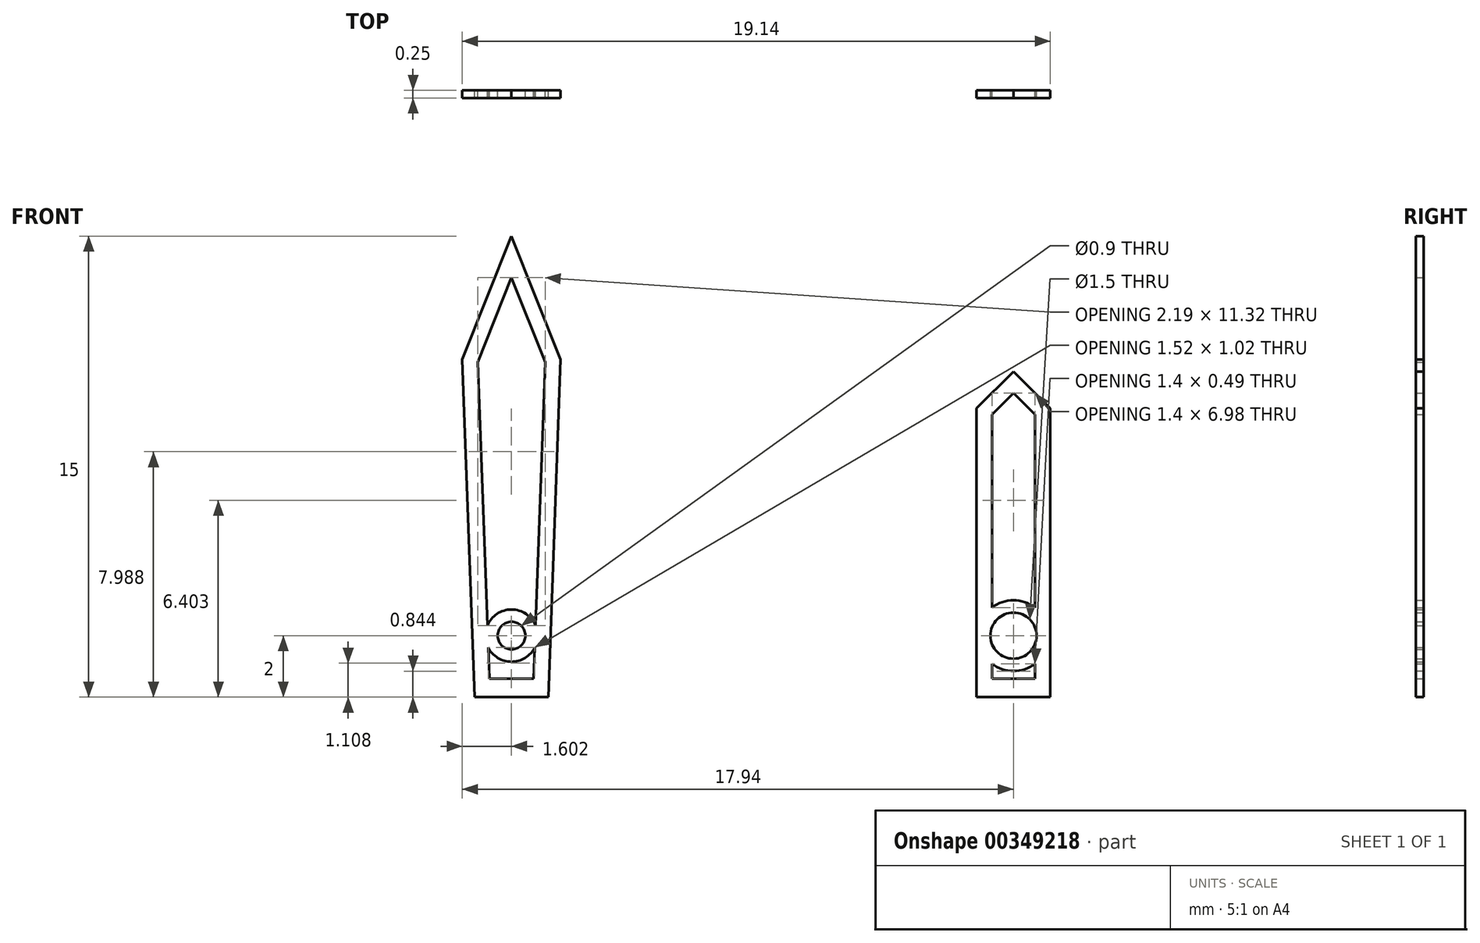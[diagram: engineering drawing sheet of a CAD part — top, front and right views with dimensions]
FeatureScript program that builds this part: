
annotation { "Feature Type Name" : "Feature", "Feature Type Description" : "" }
export const myFeature = defineFeature(function(context is Context, id is Id, definition is map)
    precondition{}
    {
        {
            var Q0;
            Q0=qCreatedBy(makeId("Front.planeOp"),FACE);
            var sketch = newSketch(context, id + "F0", { "sketchPlane" : qUnion([Q0])});
            skLineSegment(sketch, "E0", {"start": v(-36.59, 13) * mm, "end": v(-34.99, 8.98) * mm});
            skCircle(sketch, "E1", {"center": v(-36.59, 0) * mm, "radius": 0.45 * mm});
            skCircle(sketch, "E2.0", {"center": v(-36.59, 0) * mm, "radius": 0.85 * mm});
            skCircle(sketch, "E3", {"center": v(-20.25, 0) * mm, "radius": 0.75 * mm});
            skCircle(sketch, "E4", {"center": v(-28.42, 0) * mm, "radius": 0.35 * mm});
            skCircle(sketch, "E5", {"center": v(-28.42, 0) * mm, "radius": 0.75 * mm});
            skLineSegment(sketch, "E6", {"start": v(-20.25, 0) * mm, "end": v(-36.59, 0) * mm});
            skLineSegment(sketch, "E7", {"start": v(-36.59, 13) * mm, "end": v(-36.59, 0) * mm});
            skLineSegment(sketch, "E8.MirrorCS", {"start": v(-36.59, 13) * mm, "end": v(-38.19, 8.98) * mm});
            skLineSegment(sketch, "E9", {"start": v(-28.42, 0) * mm, "end": v(-28.42, 13) * mm});
            skLineSegment(sketch, "E10.0", {"start": v(-28.12, 0) * mm, "end": v(-28.12, 13) * mm});
            skLineSegment(sketch, "E11.MirrorCS", {"start": v(-28.72, 0) * mm, "end": v(-28.72, 13) * mm});
            skLineSegment(sketch, "E12", {"start": v(-28.72, 13) * mm, "end": v(-28.12, 13) * mm});
            skLineSegment(sketch, "E13.MirrorCS", {"start": v(-28.12, 0) * mm, "end": v(-28.12, -13) * mm});
            skLineSegment(sketch, "E14.MirrorCS", {"start": v(-28.72, 0) * mm, "end": v(-28.72, -13) * mm});
            skLineSegment(sketch, "E15.MirrorCS", {"start": v(-28.72, -13) * mm, "end": v(-28.12, -13) * mm});
            skLineSegment(sketch, "E16", {"start": v(-28.42, 0) * mm, "end": v(-28.42, -13) * mm});
            skLineSegment(sketch, "E17", {"start": v(-19.05, 1.5) * mm, "end": v(-19.05, 7.4) * mm});
            skLineSegment(sketch, "E18", {"start": v(-19.05, 7.4) * mm, "end": v(-20.25, 8.6) * mm});
            skLineSegment(sketch, "E19", {"start": v(-20.25, 7.9) * mm, "end": v(-19.55, 7.2) * mm});
            skLineSegment(sketch, "E20", {"start": v(-19.55, 7.2) * mm, "end": v(-19.55, 1.5) * mm});
            skLineSegment(sketch, "E21.MirrorCS", {"start": v(-20.25, 7.9) * mm, "end": v(-20.95, 7.2) * mm});
            skLineSegment(sketch, "E22.MirrorCS", {"start": v(-21.45, 7.4) * mm, "end": v(-20.25, 8.6) * mm});
            skLineSegment(sketch, "E23.MirrorCS", {"start": v(-20.95, 7.2) * mm, "end": v(-20.95, 1.5) * mm});
            skLineSegment(sketch, "E24.MirrorCS", {"start": v(-21.45, 1.5) * mm, "end": v(-21.45, 7.4) * mm});
            skLineSegment(sketch, "E25.bottom", {"start": v(-26.16, 11.7) * mm, "end": v(-23.16, 11.7) * mm});
            skLineSegment(sketch, "E25.top", {"start": v(-26.16, 11.1) * mm, "end": v(-23.16, 11.1) * mm});
            skLineSegment(sketch, "E25.left", {"start": v(-26.16, 11.7) * mm, "end": v(-26.16, 11.1) * mm});
            skLineSegment(sketch, "E25.right", {"start": v(-23.16, 11.7) * mm, "end": v(-23.16, 11.1) * mm});
            skLineSegment(sketch, "E26.bottom", {"start": v(-26.16, 10.1) * mm, "end": v(-23.16, 10.1) * mm});
            skLineSegment(sketch, "E26.top", {"start": v(-26.16, 9.5) * mm, "end": v(-23.16, 9.5) * mm});
            skLineSegment(sketch, "E26.left", {"start": v(-26.16, 10.1) * mm, "end": v(-26.16, 9.5) * mm});
            skLineSegment(sketch, "E26.right", {"start": v(-23.16, 10.1) * mm, "end": v(-23.16, 9.5) * mm});
            skLineSegment(sketch, "E27", {"start": v(-20.25, -2) * mm, "end": v(-19.05, -2) * mm});
            skLineSegment(sketch, "E28", {"start": v(-19.05, -2) * mm, "end": v(-19.05, 1.5) * mm});
            skLineSegment(sketch, "E29.0", {"start": v(-20.25, -1.4) * mm, "end": v(-19.05, -1.4) * mm});
            skLineSegment(sketch, "E30", {"start": v(-19.55, 0.27) * mm, "end": v(-19.55, 1.5) * mm});
            skLineSegment(sketch, "E31", {"start": v(-19.55, -0.27) * mm, "end": v(-19.55, -1.4) * mm});
            skLineSegment(sketch, "E32.MirrorCS", {"start": v(-20.95, 0.27) * mm, "end": v(-20.95, 1.5) * mm});
            skLineSegment(sketch, "E33.MirrorCS", {"start": v(-21.45, -2) * mm, "end": v(-21.45, 1.5) * mm});
            skLineSegment(sketch, "E34.MirrorCS", {"start": v(-20.95, -0.27) * mm, "end": v(-20.95, -1.4) * mm});
            skLineSegment(sketch, "E35.MirrorCS", {"start": v(-20.25, -1.4) * mm, "end": v(-21.45, -1.4) * mm});
            skLineSegment(sketch, "E36.MirrorCS", {"start": v(-20.25, -2) * mm, "end": v(-21.45, -2) * mm});
            skCircle(sketch, "E37", {"center": v(-20.25, 0) * mm, "radius": 1.15 * mm});
            skLineSegment(sketch, "E38", {"start": v(-36.59, -2) * mm, "end": v(-35.39, -2) * mm});
            skLineSegment(sketch, "E39", {"start": v(-34.99, 8.98) * mm, "end": v(-35.39, -2) * mm});
            skLineSegment(sketch, "E40.0", {"start": v(-36.59, -1.4) * mm, "end": v(-35.39, -1.4) * mm});
            skLineSegment(sketch, "E41", {"start": v(-35.5, 8.9) * mm, "end": v(-36.59, 11.65) * mm});
            skLineSegment(sketch, "E42", {"start": v(-35.5, 8.9) * mm, "end": v(-35.8, 0.33) * mm});
            skLineSegment(sketch, "E43", {"start": v(-35.83, -0.38) * mm, "end": v(-35.87, -1.4) * mm});
            skLineSegment(sketch, "E44.MirrorCS", {"start": v(-37.68, 8.9) * mm, "end": v(-36.59, 11.65) * mm});
            skLineSegment(sketch, "E45.MirrorCS", {"start": v(-37.68, 8.9) * mm, "end": v(-37.37, 0.33) * mm});
            skLineSegment(sketch, "E46.MirrorCS", {"start": v(-38.19, 8.98) * mm, "end": v(-37.79, -2) * mm});
            skLineSegment(sketch, "E47.MirrorCS", {"start": v(-36.59, -1.4) * mm, "end": v(-37.79, -1.4) * mm});
            skLineSegment(sketch, "E48.MirrorCS", {"start": v(-36.59, -2) * mm, "end": v(-37.79, -2) * mm});
            skLineSegment(sketch, "E49.MirrorCS", {"start": v(-37.35, -0.38) * mm, "end": v(-37.3, -1.4) * mm});
            skLineSegment(sketch, "E50", {"start": v(-37.68, 8.9) * mm, "end": v(-35.5, 8.9) * mm});
            skLineSegment(sketch, "E51", {"start": v(-20.95, 7.2) * mm, "end": v(-19.55, 7.2) * mm});
            skSolve(sketch);
        }
        {
            var Q0;
            Q0=qSketchRegion(id+"F0",true);
            var Q1;
            {var subQ0=sQuery(id+"F0.wireOp",EDGE,"d177a6a1-e401-462f-85d2-7b86f48335750.MirrorCS");var subQ1=sQuery(id+"F0.wireOp",EDGE,"215cdf59-a4c0-4674-9381-4349cfd28c600.MirrorCS");var subQ2=makeQuery(id+"F0.imprint","INTERSECT",VERTEX,{"derivedFrom":[subQ1,subQ0]});Q1=makeQuery(id+"F0.imprint","IMPRINT",FACE,{"disambiguationData":[TD([[makeQuery(id+"F0.imprint","IMPRINT",EDGE,{"disambiguationData":[TD([[subQ2,1.0]])],"derivedFrom":subQ1}),1.0]])]});}
            var Q2;
            {var subQ0=sQuery(id+"F0.wireOp",EDGE,"RracIFim-sfU7-J9re-uFhn-TZIEqMmSXRwO");var subQ1=sQuery(id+"F0.wireOp",EDGE,"TZlwwtPB-qzDZ-59c8-vJeO-k9AsrddVfFom");var subQ2=makeQuery(id+"F0.imprint","INTERSECT",VERTEX,{"derivedFrom":[subQ1,subQ0]});Q2=makeQuery(id+"F0.imprint","IMPRINT",FACE,{"disambiguationData":[TD([[makeQuery(id+"F0.imprint","IMPRINT",EDGE,{"disambiguationData":[TD([[subQ2,-1.0]])],"derivedFrom":subQ1}),1.0]])]});}
            var Q3;
            {var subQ5=sQuery(id+"F0.wireOp",EDGE,"qfoWTzAd-6RBR-ef4f-ruon-Lh11K5Xnfe9l");Q3=makeQuery(id+"F0.imprint","IMPRINT",FACE,{"disambiguationData":[TD([[makeQuery(id+"F0.imprint","IMPRINT",EDGE,{"derivedFrom":subQ5}),-1.0]])]});}
            var Q4;
            {var subQ6=sQuery(id+"F0.wireOp",EDGE,"vC55PCEN-Tw6F-4sRd-shy5-grdwKRQEr6wB");Q4=makeQuery(id+"F0.imprint","IMPRINT",FACE,{"disambiguationData":[TD([[makeQuery(id+"F0.imprint","IMPRINT",EDGE,{"derivedFrom":subQ6}),-1.0]])]});}
            var Q5;
            {var subQ0=sQuery(id+"F0.wireOp",EDGE,"E32.MirrorCS");var subQ1=sQuery(id+"F0.wireOp",EDGE,"E3");var subQ2=makeQuery(id+"F0.imprint","INTERSECT",VERTEX,{"derivedFrom":[subQ1,subQ0]});Q5=makeQuery(id+"F0.imprint","IMPRINT",FACE,{"disambiguationData":[TD([[makeQuery(id+"F0.imprint","IMPRINT",EDGE,{"disambiguationData":[TD([[subQ2,1.0]])],"derivedFrom":subQ1}),-1.0]])]});}
            var Q6;
            {var subQ0=sQuery(id+"F0.wireOp",EDGE,"E30");var subQ1=sQuery(id+"F0.wireOp",EDGE,"E3");var subQ2=makeQuery(id+"F0.imprint","INTERSECT",VERTEX,{"derivedFrom":[subQ1,subQ0]});Q6=makeQuery(id+"F0.imprint","IMPRINT",FACE,{"disambiguationData":[TD([[makeQuery(id+"F0.imprint","IMPRINT",EDGE,{"disambiguationData":[TD([[subQ2,-1.0]])],"derivedFrom":subQ1}),-1.0]])]});}
            var Q7;
            {var subQ0=sQuery(id+"F0.wireOp",EDGE,"E30");var subQ1=sQuery(id+"F0.wireOp",EDGE,"E3");var subQ2=makeQuery(id+"F0.imprint","INTERSECT",VERTEX,{"derivedFrom":[subQ1,subQ0]});Q7=makeQuery(id+"F0.imprint","IMPRINT",FACE,{"disambiguationData":[TD([[makeQuery(id+"F0.imprint","IMPRINT",EDGE,{"disambiguationData":[TD([[subQ2,1.0]])],"derivedFrom":subQ1}),-1.0]])]});}
            var Q8;
            {var subQ0=sQuery(id+"F0.wireOp",EDGE,"E31");var subQ1=sQuery(id+"F0.wireOp",EDGE,"E3");var subQ2=makeQuery(id+"F0.imprint","INTERSECT",VERTEX,{"derivedFrom":[subQ1,subQ0]});Q8=makeQuery(id+"F0.imprint","IMPRINT",FACE,{"disambiguationData":[TD([[makeQuery(id+"F0.imprint","IMPRINT",EDGE,{"disambiguationData":[TD([[subQ2,1.0]])],"derivedFrom":subQ1}),-1.0]])]});}
            var Q9;
            {var subQ0=sQuery(id+"F0.wireOp",EDGE,"E34.MirrorCS");var subQ1=sQuery(id+"F0.wireOp",EDGE,"E3");var subQ2=makeQuery(id+"F0.imprint","INTERSECT",VERTEX,{"derivedFrom":[subQ1,subQ0]});Q9=makeQuery(id+"F0.imprint","IMPRINT",FACE,{"disambiguationData":[TD([[makeQuery(id+"F0.imprint","IMPRINT",EDGE,{"disambiguationData":[TD([[subQ2,1.0]])],"derivedFrom":subQ1}),-1.0]])]});}
            var Q10;
            {var subQ0=sQuery(id+"F0.wireOp",EDGE,"E32.MirrorCS");var subQ1=sQuery(id+"F0.wireOp",EDGE,"E3");var subQ2=makeQuery(id+"F0.imprint","INTERSECT",VERTEX,{"derivedFrom":[subQ1,subQ0]});Q10=makeQuery(id+"F0.imprint","IMPRINT",FACE,{"disambiguationData":[TD([[makeQuery(id+"F0.imprint","IMPRINT",EDGE,{"disambiguationData":[TD([[subQ2,-1.0]])],"derivedFrom":subQ1}),-1.0]])]});}
            var Q11;
            {var subQ3=sQuery(id+"F0.wireOp",EDGE,"E6");var subQ4=sQuery(id+"F0.wireOp",EDGE,"E1");var subQ5=makeQuery(id+"F0.imprint","INTERSECT",VERTEX,{"derivedFrom":[subQ4,subQ3]});Q11=makeQuery(id+"F0.imprint","IMPRINT",FACE,{"disambiguationData":[TD([[makeQuery(id+"F0.imprint","IMPRINT",EDGE,{"disambiguationData":[TD([[subQ5,1.0]])],"derivedFrom":subQ4}),-1.0]])]});}
            var Q12;
            {var subQ0=sQuery(id+"F0.wireOp",EDGE,"E6");var subQ1=sQuery(id+"F0.wireOp",EDGE,"E1");var subQ2=makeQuery(id+"F0.imprint","INTERSECT",VERTEX,{"derivedFrom":[subQ1,subQ0]});Q12=makeQuery(id+"F0.imprint","IMPRINT",FACE,{"disambiguationData":[TD([[makeQuery(id+"F0.imprint","IMPRINT",EDGE,{"disambiguationData":[TD([[subQ2,-1.0]])],"derivedFrom":subQ1}),-1.0]])]});}
            extrude(context, id + "F1", {"entities" : qUnion([Q0, Q1, Q2, Q3, Q4, Q5, Q6, Q7, Q8, Q9, Q10, Q11, Q12]), "depth" : .25 * mm});
        }
        {
            var Q0;
            Q0=makeQuery(id+"F1.opExtrude","SWEPT_BODY",BODY,{"disambiguationData":[OSD([sQuery(id+"F0.wireOp",EDGE,"E25.bottom"),sQuery(id+"F0.wireOp",EDGE,"E25.top"),sQuery(id+"F0.wireOp",EDGE,"E25.left"),sQuery(id+"F0.wireOp",EDGE,"E25.right")])]});
            var Q1;
            Q1=makeQuery(id+"F1.opExtrude","SWEPT_BODY",BODY,{"disambiguationData":[OSD([sQuery(id+"F0.wireOp",EDGE,"E26.bottom"),sQuery(id+"F0.wireOp",EDGE,"E26.top"),sQuery(id+"F0.wireOp",EDGE,"E26.left"),sQuery(id+"F0.wireOp",EDGE,"E26.right")])]});
            var Q2;
            Q2=makeQuery(id+"F1.opExtrude","SWEPT_BODY",BODY,{"disambiguationData":[OSD([sQuery(id+"F0.wireOp",EDGE,"E4"),sQuery(id+"F0.wireOp",EDGE,"E5"),sQuery(id+"F0.wireOp",EDGE,"E10.0"),sQuery(id+"F0.wireOp",EDGE,"E11.MirrorCS"),sQuery(id+"F0.wireOp",EDGE,"E12"),sQuery(id+"F0.wireOp",EDGE,"E13.MirrorCS"),sQuery(id+"F0.wireOp",EDGE,"E14.MirrorCS"),sQuery(id+"F0.wireOp",EDGE,"E15.MirrorCS")])]});
            deleteBodies(context, id + "F2", {"entities" : qUnion([Q0, Q1, Q2])});
        }
    });
